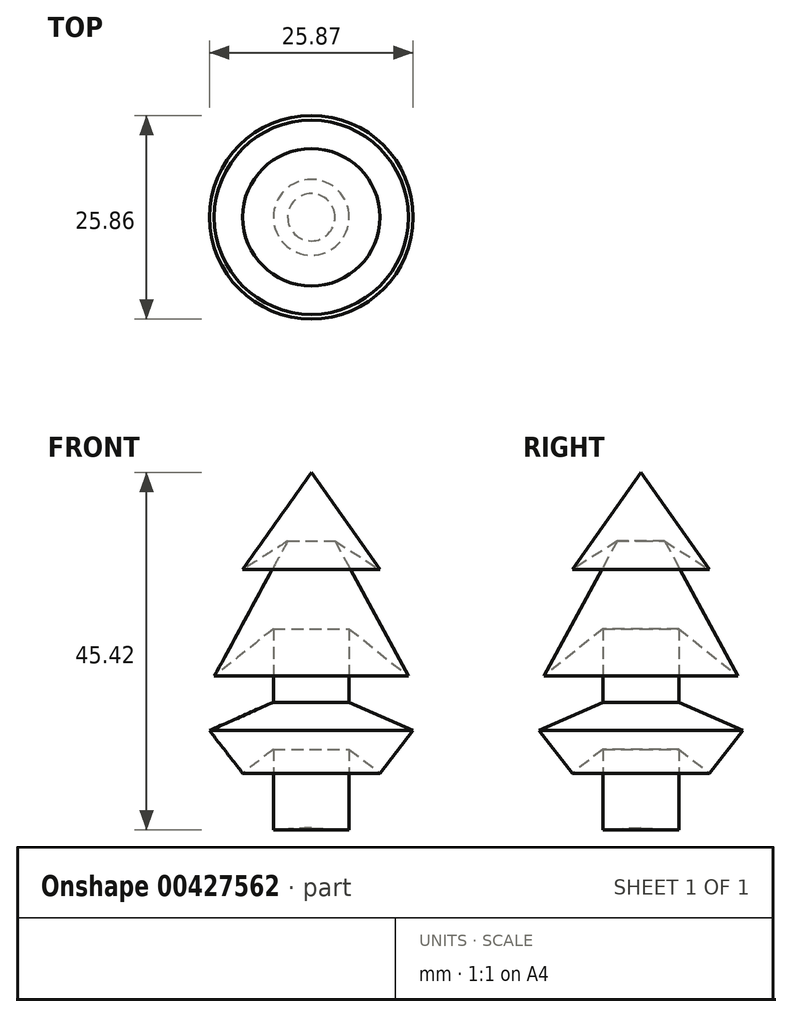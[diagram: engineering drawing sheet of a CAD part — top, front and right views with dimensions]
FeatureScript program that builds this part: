
annotation { "Feature Type Name" : "Feature", "Feature Type Description" : "" }
export const myFeature = defineFeature(function(context is Context, id is Id, definition is map)
    precondition{}
    {
        {
            var Q0;
            Q0=qCreatedBy(makeId("Front.planeOp"),FACE);
            var sketch = newSketch(context, id + "F0", { "sketchPlane" : qUnion([Q0])});
            skLineSegment(sketch, "E0", {"start": v(-27.97, 8.42) * mm, "end": v(-27.97, 53.54) * mm});
            skLineSegment(sketch, "E1", {"start": v(-27.97, 53.54) * mm, "end": v(-36.7, 41.2) * mm});
            skLineSegment(sketch, "E2", {"start": v(-36.7, 41.2) * mm, "end": v(-30.98, 44.82) * mm});
            skLineSegment(sketch, "E3", {"start": v(-30.98, 44.82) * mm, "end": v(-40.3, 27.67) * mm});
            skLineSegment(sketch, "E4", {"start": v(-40.3, 27.67) * mm, "end": v(-32.79, 33.69) * mm});
            skLineSegment(sketch, "E5", {"start": v(-32.79, 33.69) * mm, "end": v(-32.79, 24.36) * mm});
            skLineSegment(sketch, "E6", {"start": v(-32.79, 24.36) * mm, "end": v(-40.9, 20.75) * mm});
            skLineSegment(sketch, "E7", {"start": v(-40.9, 20.75) * mm, "end": v(-36.7, 15.34) * mm});
            skLineSegment(sketch, "E8", {"start": v(-36.7, 15.34) * mm, "end": v(-32.79, 18.38) * mm});
            skLineSegment(sketch, "E9", {"start": v(-32.79, 18.38) * mm, "end": v(-32.79, 8.12) * mm});
            skLineSegment(sketch, "E10", {"start": v(-32.79, 8.12) * mm, "end": v(-27.97, 8.42) * mm});
            skSolve(sketch);
        }
        {
            var Q0;
            Q0=makeQuery(id+"F0.imprint","IMPRINT",FACE,{"disambiguationData":[TD([[makeQuery(id+"F0.imprint","IMPRINT",EDGE,{"derivedFrom":sQuery(id+"F0.wireOp",EDGE,"E0")}),1.0]])]});
            var Q1;
            Q1=sQuery(id+"F0.wireOp",EDGE,"E0");
            revolve(context, id + "F1", {"entities" : qUnion([Q0]), "axis" : qUnion([Q1]), "revolveType" : RevolveType.FULL});
        }
    });
